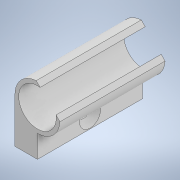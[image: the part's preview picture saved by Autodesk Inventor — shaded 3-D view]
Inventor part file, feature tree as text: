
AUTODESK INVENTOR PART (.ipt)
format: ipt  version: 2022.1 (Build 261234020, 234B)  size: 296,448 bytes
history: native  units: in
note: dims shown in document units (in); Inventor stores cm internally (conversion verified against a paired STEP export)
features: sketch x4, extrude x3, hole x1
ambient origin geometry x8: Origin, YZ Plane, XZ Plane, XY Plane, X Axis, Y Axis, Z Axis, Center Point
bodies: Body1 (feature_tree)
feature tree (8):
  extrude  "Extrusion3"  Depth=0.05in
  extrude  "Extrusion4"  Depth=0.3in
  hole  "Hole1"  [1 undecoded]
  extrude  "Text"  Depth=0.045in
  sketch  "Sketch4"  dims[d10=0.5in d11=0.05in]
  sketch  "Sketch5"  dims[d12=45.0deg d13=0.3in]
  sketch  "Sketch6"  dims[d14=1.4in d15=0.0in]
  sketch  "Sketch10"  dims[d16=0.3in d17=1.4in d18=0.0in d19=0.138in d20=0.75in d21=0.28in d22=0.25in d23=0.5635in d24=0.29in d25=0.0in d28=0.045in d29=0.0in d30=0.15in d31=0.0in]
note: 1 required parameter value undecoded (feature->parameter linkage not recoverable at this tier; creation-order binding heuristic only, values carry confidence <= 0.55)
